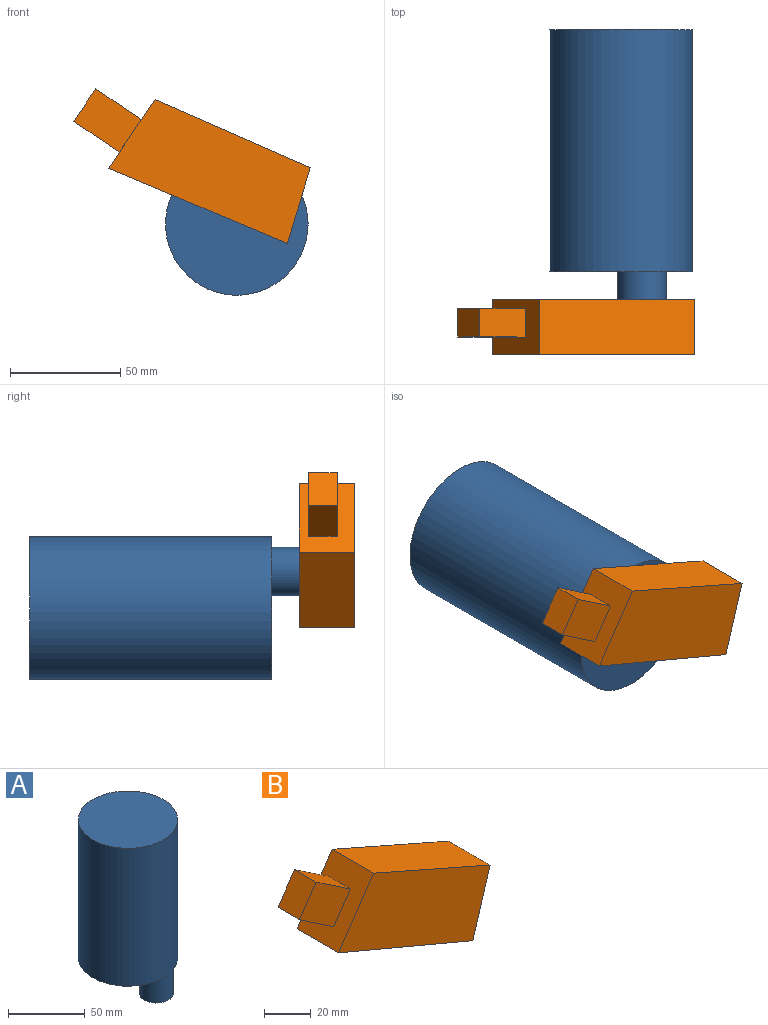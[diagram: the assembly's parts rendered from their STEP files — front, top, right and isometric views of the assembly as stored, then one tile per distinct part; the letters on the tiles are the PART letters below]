
ASSEMBLY  parts=2 mates=1
PART A: 5 faces, bbox 64.6x64.6x134.8 mm
  f0: cylinder r=32.32mm len=109.8mm, axis (0,0,-1), area 22296.5mm2, adj f1,f2
  f1: plane 64.64x64.64mm, normal (0,0,1), area 3281.4mm2, adj f0
  f2: plane 64.64x64.64mm, normal (0,0,-1), area 2901.4mm2, adj f0,f3
  f3: cylinder r=11mm len=25mm, axis (0,0,1), area 1727.5mm2, adj f2,f4
  f4: plane 22x22mm, normal (0,0,-1), area 380mm2, adj f3
PART B: 15 faces, bbox 107.2x25x70.2 mm
  f0: plane 70.34x30.92mm, normal (0.4,0,0.92), area 1920.9mm2, adj f1,f3,f4,f5
  f1: plane 31.09x25mm, normal (-0.83,0,0.56), area 708.7mm2, adj f0,f2,f4,f5,f6,f7,f8,f9
  f2: plane 81.04x34.15mm, normal (-0.39,0,-0.92), area 2198.6mm2, adj f1,f3,f4,f5
  f3: plane 34.32x25mm, normal (0.96,0,-0.29), area 896.3mm2, adj f0,f2,f4,f5
  f4: plane 91.41x65.24mm, normal (0,-1,0), area 2986.9mm2, adj f0,f1,f2,f3
  f5: plane 91.41x65.24mm, normal (0,1,0), area 2939.4mm2, adj f0,f1,f2,f3,f12,f14
  f6: plane 20.7x14.02mm, normal (0.56,0,0.83), area 323.4mm2, adj f1,f7,f9,f10
  f7: plane 30.68x28.76mm, normal (0,1,0), area 444.9mm2, adj f1,f6,f8,f10
  f8: plane 20.7x14.02mm, normal (-0.56,0,-0.83), area 323.4mm2, adj f1,f7,f9,f10
  f9: plane 30.68x28.76mm, normal (0,-1,0), area 444.9mm2, adj f1,f6,f8,f10
  f10: plane 14.73x12.94mm, normal (-0.83,0,0.56), area 230.2mm2, adj f6,f7,f8,f9
  f11: cone r=0mm half-angle=59deg, axis (0,1,0), area 27.7mm2, adj f12
  f12: cylinder r=2.75mm len=12mm, axis (0,1,0), area 207.3mm2, adj f5,f11
  f13: cone r=0mm half-angle=59deg, axis (0,1,0), area 27.7mm2, adj f14
  f14: cylinder r=2.75mm len=12mm, axis (0,1,0), area 207.3mm2, adj f5,f13
PLACE A rot(axis=(-1,0,0),90deg) t=(-35.19,-21.13,-15.94)mm
PLACE B t=(-37.83,-33.63,-17.68)mm fixed
MATE revolute A.f3 <-> B.f13  axis (0,1,0) through (-25.65,-33.63,0.59)mm
